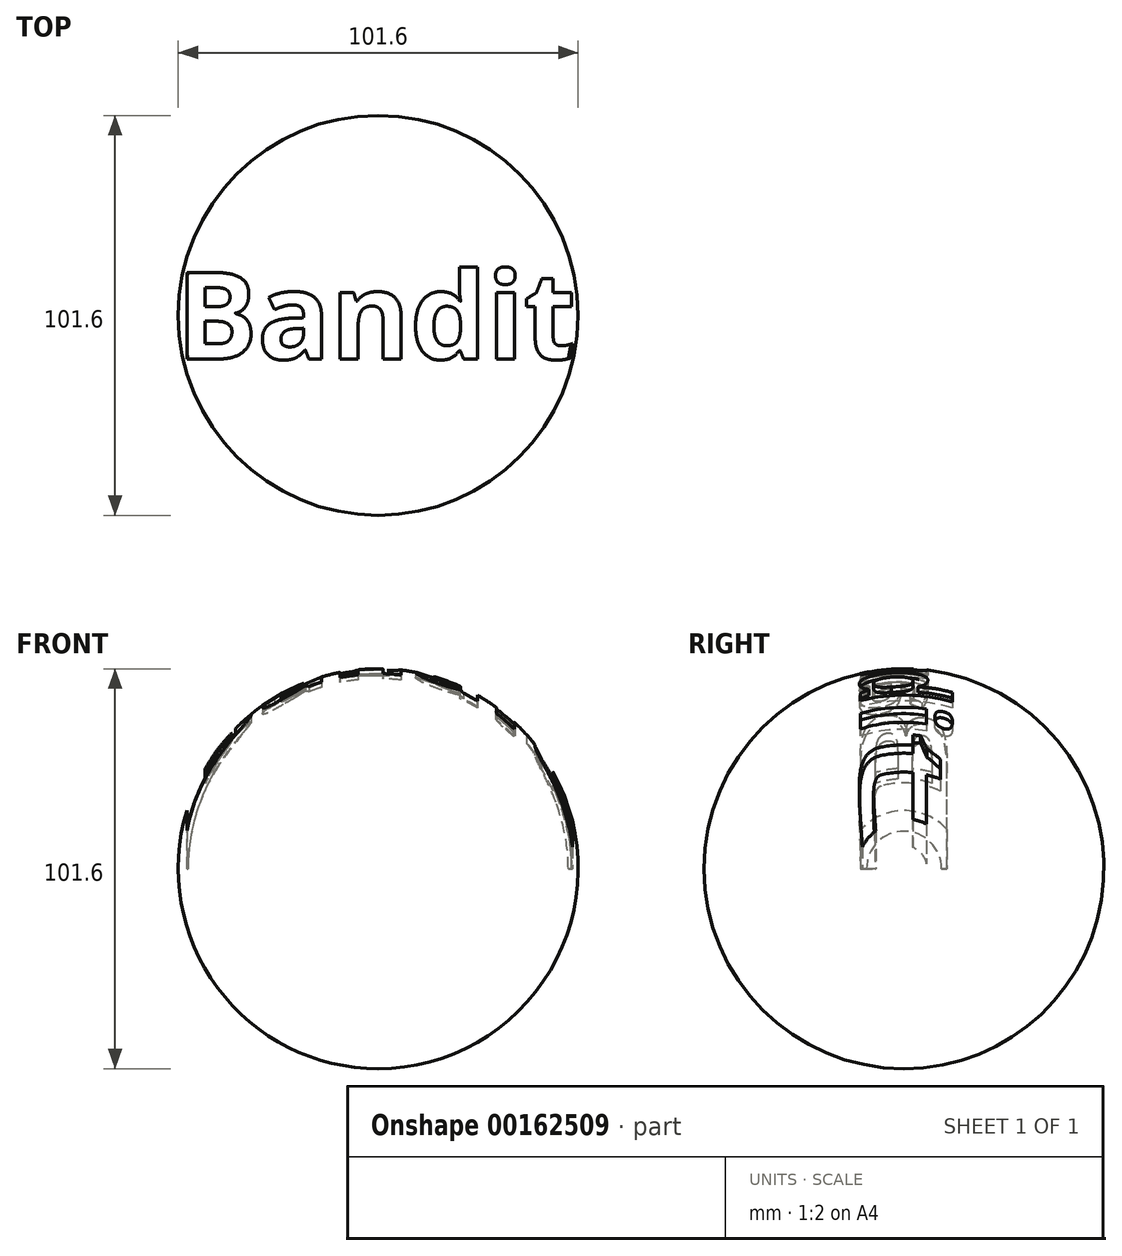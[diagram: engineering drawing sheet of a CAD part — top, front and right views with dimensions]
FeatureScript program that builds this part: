
annotation { "Feature Type Name" : "Feature", "Feature Type Description" : "" }
export const myFeature = defineFeature(function(context is Context, id is Id, definition is map)
    precondition{}
    {
        {
            var Q0;
            Q0=qCreatedBy(makeId("Front.planeOp"),FACE);
            var sketch = newSketch(context, id + "F0", { "sketchPlane" : qUnion([Q0])});
            skArc(sketch, "E0.0", {"start": v(0, 50.8) * mm, "mid": v(-50.8, 0) * mm, "end": v(0, -50.8) * mm});
            skLineSegment(sketch, "E1", {"start": v(0, 50.8) * mm, "end": v(0, -50.8) * mm});
            skPoint(sketch, "E2.end.orphan", {"position": v(0, -60.13) * mm});
            skSolve(sketch);
        }
        {
            var Q0;
            Q0=makeQuery(id+"F0.imprint","IMPRINT",FACE,{"disambiguationData":[TD([[makeQuery(id+"F0.imprint","IMPRINT",EDGE,{"derivedFrom":sQuery(id+"F0.wireOp",EDGE,"E0.0")}),1.0]])]});
            var Q1;
            Q1=sQuery(id+"F0.wireOp",EDGE,"E1");
            revolve(context, id + "F1", {"entities" : qUnion([Q0]), "axis" : qUnion([Q1]), "revolveType" : RevolveType.FULL});
        }
        {
            var Q0;
            Q0=qCreatedBy(makeId("Top.planeOp"),FACE);
            var sketch = newSketch(context, id + "F2", { "sketchPlane" : qUnion([Q0])});
            skText(sketch, "E3", { "text": "Bandit\n", "fontName": "OpenSans-Bold.ttf"});
            const initialGuessF2  = {"E3": [-0.05137, -0.01108, 1, 0, 0.02216]};
            skSetInitialGuess(sketch, initialGuessF2);
            skSolve(sketch);
        }
        {
            var Q0;
            Q0 = qSketchRegion(id + "F2", true);
            extrude(context, id + "F3", {"entities" : qUnion([Q0]), "operationType" : NewBodyOperationType.REMOVE, "depth" : 81.28 * mm});
        }
        {
            var Q0;
            Q0=qCreatedBy(makeId("Right.planeOp"),FACE);
            var sketch = newSketch(context, id + "F4", { "sketchPlane" : qUnion([Q0])});
            skArc(sketch, "E4", {"start": v(49.53, 0) * mm, "mid": v(0, 49.53) * mm, "end": v(-49.53, 0) * mm});
            skLineSegment(sketch, "E5", {"start": v(49.53, 0) * mm, "end": v(-49.53, 0) * mm});
            skSolve(sketch);
        }
        {
            var Q0;
            Q0 = qSketchRegion(id + "F4", true);
            var Q1;
            Q1=sQuery(id+"F4.wireOp",EDGE,"E5");
            revolve(context, id + "F5", {"operationType" : NewBodyOperationType.ADD, "entities" : qUnion([Q0]), "axis" : qUnion([Q1]), "revolveType" : RevolveType.FULL});
        }
    });
